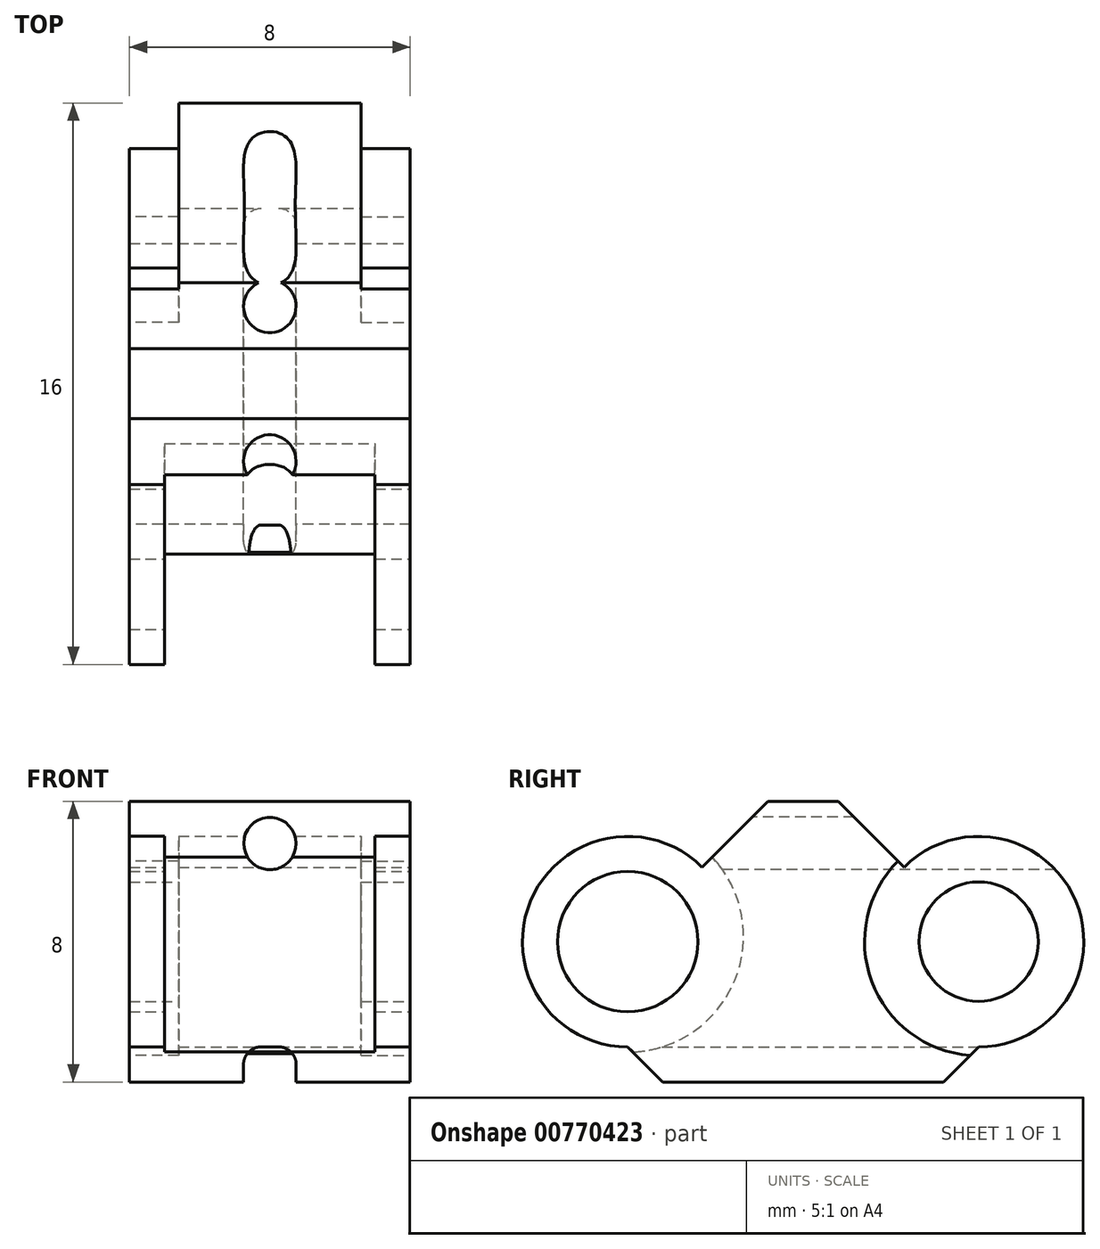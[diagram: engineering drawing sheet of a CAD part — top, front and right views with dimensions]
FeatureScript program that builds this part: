
annotation { "Feature Type Name" : "Feature", "Feature Type Description" : "" }
export const myFeature = defineFeature(function(context is Context, id is Id, definition is map)
    precondition{}
    {
        {
            var Q0;
            Q0=qCreatedBy(makeId("Top.planeOp"),FACE);
            var sketch = newSketch(context, id + "F0", { "sketchPlane" : qUnion([Q0])});
            skLineSegment(sketch, "E0.bottom", {"start": v(-4, 0) * mm, "end": v(4, 0) * mm});
            skLineSegment(sketch, "E0.top", {"start": v(-4, 10) * mm, "end": v(4, 10) * mm});
            skLineSegment(sketch, "E0.left", {"start": v(-4, 0) * mm, "end": v(-4, 10) * mm});
            skLineSegment(sketch, "E0.right", {"start": v(4, 0) * mm, "end": v(4, 10) * mm});
            skSolve(sketch);
        }
        {
            var Q0;
            Q0=makeQuery(id+"F0.imprint","IMPRINT",FACE,{"disambiguationData":[TD([[makeQuery(id+"F0.imprint","IMPRINT",EDGE,{"derivedFrom":sQuery(id+"F0.wireOp",EDGE,"E0.bottom")}),1.0]])]});
            extrude(context, id + "F1", {"entities" : qUnion([Q0]), "depth" : 8 * mm, "offsetDistance" : 25 * mm});
        }
        {
            var Q0;
            Q0=makeQuery(id+"F1.opExtrude","CAP_EDGE",EDGE,{"disambiguationData":[OSD([sQuery(id+"F0.wireOp",EDGE,"E0.bottom")])],"isStart":false});
            var Q1;
            Q1=makeQuery(id+"F1.opExtrude","CAP_EDGE",EDGE,{"disambiguationData":[OSD([sQuery(id+"F0.wireOp",EDGE,"E0.top")])],"isStart":false});
            chamfer(context, id + "F2", {"entities" : qUnion([Q0, Q1]), "width" : 4 * mm, "tangentPropagation" : true});
        }
        {
            var Q0;
            Q0=qCreatedBy(makeId("Right.planeOp"),FACE);
            var sketch = newSketch(context, id + "F3", { "sketchPlane" : qUnion([Q0])});
            skLineSegment(sketch, "E1.0.0", {"start": v(10, 0) * mm, "end": v(10, 4) * mm});
            skLineSegment(sketch, "E1.0.1", {"start": v(10, 4) * mm, "end": v(6, 8) * mm});
            skLineSegment(sketch, "E1.0.2", {"start": v(6, 8) * mm, "end": v(4, 8) * mm});
            skLineSegment(sketch, "E1.0.3", {"start": v(4, 8) * mm, "end": v(0, 4) * mm});
            skLineSegment(sketch, "E1.0.4", {"start": v(0, 4) * mm, "end": v(0, 0) * mm});
            skLineSegment(sketch, "E1.0.5", {"start": v(0, 0) * mm, "end": v(10, 0) * mm});
            skCircle(sketch, "E2", {"center": v(0, 4) * mm, "radius": 3 * mm});
            skCircle(sketch, "E3", {"center": v(10, 4) * mm, "radius": 3 * mm});
            skSolve(sketch);
        }
        {
            var Q0;
            {var subQ0=sQuery(id+"F3.wireOp",EDGE,"E1.0.4");var subQ1=sQuery(id+"F3.wireOp",EDGE,"E1.0.3");var subQ2=makeQuery(id+"F3.imprint","INTERSECT",VERTEX,{"derivedFrom":[subQ1,subQ0]});Q0=makeQuery(id+"F3.imprint","IMPRINT",FACE,{"disambiguationData":[TD([[makeQuery(id+"F3.imprint","IMPRINT",EDGE,{"disambiguationData":[TD([[subQ2,1.0]])],"derivedFrom":subQ1}),-1.0]])]});}
            extrude(context, id + "F4", {"entities" : qUnion([Q0]), "operationType" : NewBodyOperationType.ADD, "endBound" : BoundingType.SYMMETRIC, "oppositeDirection" : true, "depth" : 8 * mm, "offsetDistance" : 25 * mm});
        }
        {
            var Q0;
            {var subQ0=sQuery(id+"F3.wireOp",EDGE,"E1.0.1");var subQ1=sQuery(id+"F3.wireOp",EDGE,"E1.0.0");var subQ2=makeQuery(id+"F3.imprint","INTERSECT",VERTEX,{"derivedFrom":[subQ1,subQ0]});Q0=makeQuery(id+"F3.imprint","IMPRINT",FACE,{"disambiguationData":[TD([[makeQuery(id+"F3.imprint","IMPRINT",EDGE,{"disambiguationData":[TD([[subQ2,1.0]])],"derivedFrom":subQ1}),-1.0]])]});}
            extrude(context, id + "F5", {"entities" : qUnion([Q0]), "operationType" : NewBodyOperationType.ADD, "endBound" : BoundingType.SYMMETRIC, "oppositeDirection" : true, "depth" : 6 * mm, "offsetDistance" : 25 * mm});
        }
        {
            var Q0;
            Q0=qCreatedBy(makeId("Right.planeOp"),FACE);
            var sketch = newSketch(context, id + "F6", { "sketchPlane" : qUnion([Q0])});
            skCircle(sketch, "E4", {"center": v(0, 4.15) * mm, "radius": 3.3 * mm});
            skSolve(sketch);
        }
        {
            var Q0;
            Q0=makeQuery(id+"F6.imprint","IMPRINT",FACE,{"disambiguationData":[TD([[makeQuery(id+"F6.imprint","IMPRINT",EDGE,{"derivedFrom":sQuery(id+"F6.wireOp",EDGE,"E4")}),1.0]])]});
            extrude(context, id + "F7", {"entities" : qUnion([Q0]), "operationType" : NewBodyOperationType.REMOVE, "endBound" : BoundingType.SYMMETRIC, "oppositeDirection" : true, "depth" : 6 * mm, "offsetDistance" : 25 * mm});
        }
        {
            var Q0;
            Q0=makeQuery(id+"F4.boolean.opBoolean","MERGE",FACE,{"derivedFrom":[makeQuery(id+"F1.opExtrude","SWEPT_FACE",FACE,{"disambiguationData":[OSD([sQuery(id+"F0.wireOp",EDGE,"E0.left")])]}),makeQuery(id+"F4.opExtrude","CAP_FACE",FACE,{"disambiguationData":[OSD([sQuery(id+"F3.wireOp",EDGE,"E1.0.3"),sQuery(id+"F3.wireOp",EDGE,"E1.0.4"),sQuery(id+"F3.wireOp",EDGE,"E2")])],"isStart":false})]});
            var sketch = newSketch(context, id + "F8", { "sketchPlane" : qUnion([Q0])});
            skCircle(sketch, "E5", {"center": v(-10, 4) * mm, "radius": 3.25 * mm});
            skSolve(sketch);
        }
        {
            var Q0;
            {var subQ0=sQuery(id+"F8.wireOp",EDGE,"E5");var subQ1=sQuery(id+"F0.wireOp",EDGE,"E0.left");var subQ2=sQuery(id+"F0.wireOp",EDGE,"E0.top");var subQ3=makeQuery(id+"F1.opExtrude","SWEPT_EDGE",EDGE,{"disambiguationData":[OSD([subQ2,subQ1])]});var subQ4=makeQuery(id+"F8.imprint","INTERSECT",VERTEX,{"derivedFrom":[subQ3,subQ0]});Q0=makeQuery(id+"F8.imprint","IMPRINT",FACE,{"disambiguationData":[TD([[makeQuery(id+"F8.imprint","IMPRINT",EDGE,{"disambiguationData":[TD([[subQ4,1.0]])],"derivedFrom":subQ0}),1.0]])]});}
            var Q1;
            {var subQ0=sQuery(id+"F8.wireOp",EDGE,"E5");var subQ1=sQuery(id+"F0.wireOp",EDGE,"E0.left");var subQ2=sQuery(id+"F0.wireOp",EDGE,"E0.top");var subQ3=makeQuery(id+"F1.opExtrude","SWEPT_EDGE",EDGE,{"disambiguationData":[OSD([subQ2,subQ1])]});var subQ4=makeQuery(id+"F8.imprint","INTERSECT",VERTEX,{"derivedFrom":[subQ3,subQ0]});Q1=makeQuery(id+"F8.imprint","IMPRINT",FACE,{"disambiguationData":[TD([[makeQuery(id+"F8.imprint","IMPRINT",EDGE,{"disambiguationData":[TD([[subQ4,-1.0]])],"derivedFrom":subQ0}),1.0]])]});}
            extrude(context, id + "F9", {"entities" : qUnion([Q0, Q1]), "operationType" : NewBodyOperationType.REMOVE, "oppositeDirection" : true, "depth" : 1.4 * mm, "offsetDistance" : 25 * mm});
        }
        {
            var Q0;
            Q0=makeQuery(id+"F1.opExtrude","SWEPT_BODY",BODY,{"disambiguationData":[OSD([sQuery(id+"F0.wireOp",EDGE,"E0.bottom"),sQuery(id+"F0.wireOp",EDGE,"E0.top"),sQuery(id+"F0.wireOp",EDGE,"E0.left"),sQuery(id+"F0.wireOp",EDGE,"E0.right")])]});
            var Q1;
            Q1=qCreatedBy(makeId("Right.planeOp"),FACE);
            mirror(context, id + "F10", {"operationType" : NewBodyOperationType.INTERSECT, "entities" : qUnion([Q0]), "mirrorPlane" : qUnion([Q1])});
        }
        {
            var Q0;
            Q0=qCreatedBy(makeId("Right.planeOp"),FACE);
            var sketch = newSketch(context, id + "F11", { "sketchPlane" : qUnion([Q0])});
            skArc(sketch, "E6.0", {"start": v(10, 1) * mm, "mid": v(12.77, 5.15) * mm, "end": v(7.88, 6.12) * mm});
            skCircle(sketch, "E7", {"center": v(10, 4) * mm, "radius": 1.7 * mm});
            skSolve(sketch);
        }
        {
            var Q0;
            Q0=qSketchRegion(id+"F11",true);
            extrude(context, id + "F12", {"entities" : qUnion([Q0]), "operationType" : NewBodyOperationType.ADD, "endBound" : BoundingType.SYMMETRIC, "oppositeDirection" : true, "depth" : 8 * mm, "offsetDistance" : 25 * mm});
        }
        {
            var Q0;
            Q0=qCreatedBy(makeId("Right.planeOp"),FACE);
            var sketch = newSketch(context, id + "F13", { "sketchPlane" : qUnion([Q0])});
            skCircle(sketch, "E8.0", {"center": v(0, 4) * mm, "radius": 3 * mm});
            skCircle(sketch, "E9", {"center": v(0, 4) * mm, "radius": 2 * mm});
            skSolve(sketch);
        }
        {
            var Q0;
            Q0=makeQuery(id+"F13.imprint","IMPRINT",FACE,{"disambiguationData":[TD([[makeQuery(id+"F13.imprint","IMPRINT",EDGE,{"derivedFrom":sQuery(id+"F13.wireOp",EDGE,"E9")}),1.0]])]});
            extrude(context, id + "F14", {"entities" : qUnion([Q0]), "operationType" : NewBodyOperationType.REMOVE, "endBound" : BoundingType.SYMMETRIC, "oppositeDirection" : true, "depth" : 25 * mm, "offsetDistance" : 25 * mm});
        }
        {
            var Q0;
            Q0=makeQuery(id+"F1.opExtrude","CAP_EDGE",EDGE,{"disambiguationData":[OSD([sQuery(id+"F0.wireOp",EDGE,"E0.top")])],"isStart":true});
            var Q1;
            Q1=makeQuery(id+"F1.opExtrude","CAP_EDGE",EDGE,{"disambiguationData":[OSD([sQuery(id+"F0.wireOp",EDGE,"E0.bottom")])],"isStart":true});
            chamfer(context, id + "F15", {"entities" : qUnion([Q0, Q1]), "width" : 1 * mm, "tangentPropagation" : true});
        }
        {
            var Q0;
            Q0=makeQuery(id+"F1.opExtrude","CAP_FACE",FACE,{"disambiguationData":[OSD([sQuery(id+"F0.wireOp",EDGE,"E0.bottom"),sQuery(id+"F0.wireOp",EDGE,"E0.top"),sQuery(id+"F0.wireOp",EDGE,"E0.left"),sQuery(id+"F0.wireOp",EDGE,"E0.right")])],"isStart":true});
            var sketch = newSketch(context, id + "F16", { "sketchPlane" : qUnion([Q0])});
            skLineSegment(sketch, "E10.bottom", {"start": v(-0.75, -0.2) * mm, "end": v(0.75, -0.2) * mm});
            skLineSegment(sketch, "E10.top", {"start": v(-0.75, -10.07) * mm, "end": v(0.75, -10.07) * mm});
            skLineSegment(sketch, "E10.left", {"start": v(-0.75, -0.2) * mm, "end": v(-0.75, -10.07) * mm});
            skLineSegment(sketch, "E10.right", {"start": v(0.75, -0.2) * mm, "end": v(0.75, -10.07) * mm});
            skSolve(sketch);
        }
        {
            var Q0;
            {var subQ0=sQuery(id+"F16.wireOp",EDGE,"E10.top");Q0=makeQuery(id+"F16.imprint","IMPRINT",FACE,{"disambiguationData":[TD([[makeQuery(id+"F16.imprint","IMPRINT",EDGE,{"derivedFrom":subQ0}),1.0]])]});}
            var Q1;
            {var subQ0=sQuery(id+"F16.wireOp",EDGE,"E10.left");var subQ1=sQuery(id+"F0.wireOp",EDGE,"E0.top");var subQ2=sQuery(id+"F0.wireOp",EDGE,"E0.bottom");var subQ3=makeQuery(id+"F1.opExtrude","CAP_FACE",FACE,{"disambiguationData":[OSD([subQ2,subQ1,sQuery(id+"F0.wireOp",EDGE,"E0.left"),sQuery(id+"F0.wireOp",EDGE,"E0.right")])],"isStart":true});var subQ4=makeQuery(id+"F15.opChamfer","BLEND_EDGE",EDGE,{"blendedFrom":[makeQuery(id+"F1.opExtrude","CAP_EDGE",EDGE,{"disambiguationData":[OSD([subQ2])],"isStart":true}),subQ3],"blendedInto":[subQ3]});var subQ5=makeQuery(id+"F16.imprint","INTERSECT",VERTEX,{"derivedFrom":[subQ4,subQ0]});Q1=makeQuery(id+"F16.imprint","IMPRINT",FACE,{"disambiguationData":[TD([[makeQuery(id+"F16.imprint","IMPRINT",EDGE,{"disambiguationData":[TD([[subQ5,-1.0]])],"derivedFrom":subQ0}),1.0]])]});}
            var Q2;
            {var subQ0=sQuery(id+"F16.wireOp",EDGE,"E10.bottom");Q2=makeQuery(id+"F16.imprint","IMPRINT",FACE,{"disambiguationData":[TD([[makeQuery(id+"F16.imprint","IMPRINT",EDGE,{"derivedFrom":subQ0}),-1.0]])]});}
            extrude(context, id + "F17", {"entities" : qUnion([Q0, Q1, Q2]), "operationType" : NewBodyOperationType.REMOVE, "oppositeDirection" : true, "depth" : 1 * mm, "offsetDistance" : 25 * mm});
        }
        {
            var Q0;
            Q0=makeQuery(id+"F17.boolean.opBoolean","COPY",EDGE,{"derivedFrom":makeQuery(id+"F17.opExtrude","CAP_EDGE",EDGE,{"disambiguationData":[OSD([sQuery(id+"F16.wireOp",EDGE,"E10.left")])],"isStart":false})});
            var Q1;
            Q1=makeQuery(id+"F17.boolean.opBoolean","COPY",EDGE,{"derivedFrom":makeQuery(id+"F17.opExtrude","CAP_EDGE",EDGE,{"disambiguationData":[OSD([sQuery(id+"F16.wireOp",EDGE,"E10.right")])],"isStart":false})});
            fillet(context, id + "F18", {"entities" : qUnion([Q0, Q1]), "radius" : 0.5 * mm, "tangentPropagation" : true, "allowEdgeOverflow" : false});
        }
        {
            var Q0;
            Q0=qCreatedBy(makeId("Front.planeOp"),FACE);
            var sketch = newSketch(context, id + "F19", { "sketchPlane" : qUnion([Q0])});
            skCircle(sketch, "E11", {"center": v(0, 6.8) * mm, "radius": 0.75 * mm});
            skLineSegment(sketch, "E12.0", {"start": v(-4, 8) * mm, "end": v(4, 8) * mm});
            skSolve(sketch);
        }
        {
            var Q0;
            Q0=makeQuery(id+"F19.imprint","IMPRINT",FACE,{"disambiguationData":[TD([[makeQuery(id+"F19.imprint","IMPRINT",EDGE,{"derivedFrom":sQuery(id+"F19.wireOp",EDGE,"E11")}),1.0]])]});
            extrude(context, id + "F20", {"entities" : qUnion([Q0]), "operationType" : NewBodyOperationType.REMOVE, "oppositeDirection" : true, "depth" : 25 * mm, "offsetDistance" : 25 * mm});
        }
    });
